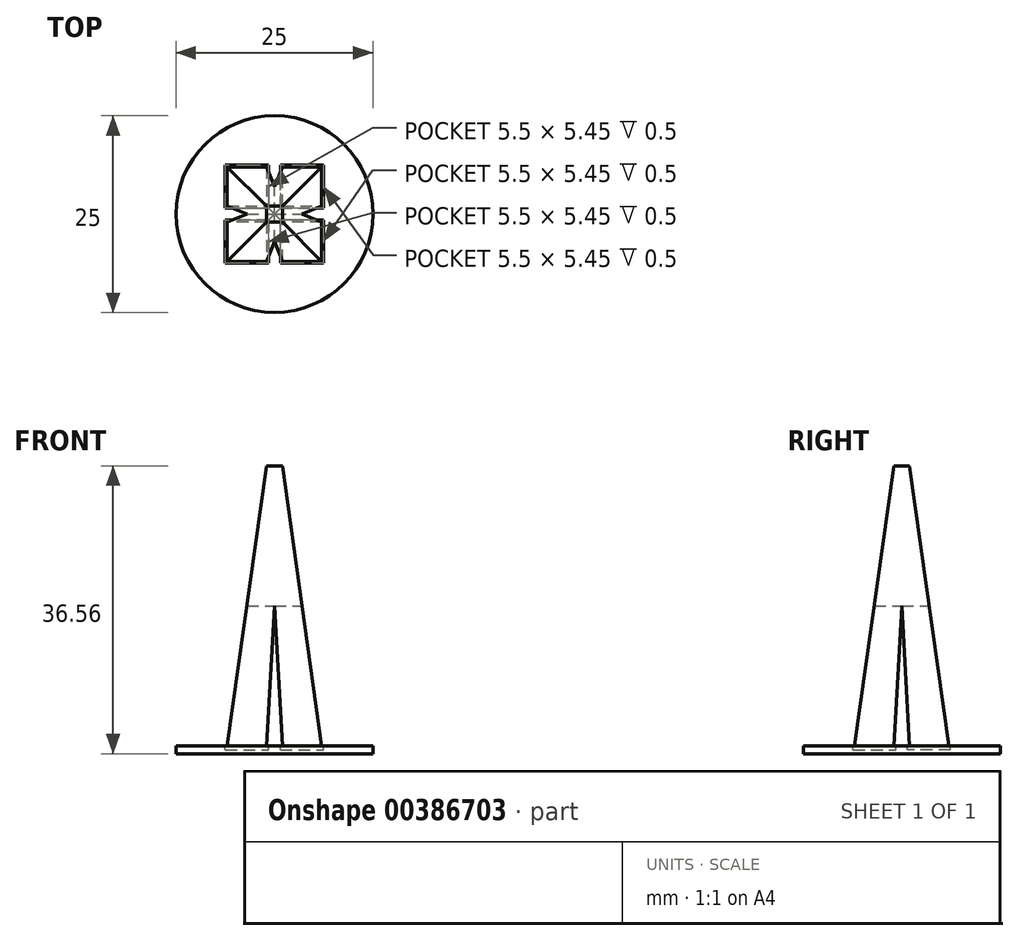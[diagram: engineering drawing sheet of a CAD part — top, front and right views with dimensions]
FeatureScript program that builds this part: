
annotation { "Feature Type Name" : "Feature", "Feature Type Description" : "" }
export const myFeature = defineFeature(function(context is Context, id is Id, definition is map)
    precondition{}
    {
        {
            var Q0;
            Q0=qCreatedBy(makeId("Top.planeOp"),FACE);
            var sketch = newSketch(context, id + "F0", { "sketchPlane" : qUnion([Q0])});
            skLineSegment(sketch, "E0.bottom", {"start": v(-6, 6) * mm, "end": v(6, 6) * mm});
            skLineSegment(sketch, "E0.top", {"start": v(-6, -6) * mm, "end": v(6, -6) * mm});
            skLineSegment(sketch, "E0.left", {"start": v(-6, 6) * mm, "end": v(-6, -6) * mm});
            skLineSegment(sketch, "E0.right", {"start": v(6, 6) * mm, "end": v(6, -6) * mm});
            skPoint(sketch, "E0.middle", {"position": v(0, 0) * mm});
            skLineSegment(sketch, "E1", {"start": v(-6, 0) * mm, "end": v(6, 0) * mm});
            skLineSegment(sketch, "E2", {"start": v(0, 6) * mm, "end": v(0, -6) * mm});
            skLineSegment(sketch, "E3", {"start": v(-1, 6) * mm, "end": v(-1, -6) * mm});
            skLineSegment(sketch, "E4", {"start": v(1, -6) * mm, "end": v(1, 6) * mm});
            skLineSegment(sketch, "E5", {"start": v(-6, 1) * mm, "end": v(6, 1) * mm});
            skLineSegment(sketch, "E6", {"start": v(6, -1) * mm, "end": v(-6, -1) * mm});
            skSolve(sketch);
        }
        {
            var Q0;
            Q0=qCreatedBy(makeId("Top.planeOp"),FACE);
            cPlane(context, id + "F1", {"entities" : qUnion([Q0]), "cplaneType" : CPlaneType.OFFSET, "offset" : 35.56 * mm, "width" : 150 * mm, "height" : 150 * mm});
        }
        {
            var Q0;
            Q0=qCreatedBy(id+"F1.planeOp",FACE);
            var sketch = newSketch(context, id + "F2", { "sketchPlane" : qUnion([Q0])});
            skLineSegment(sketch, "E7.bottom", {"start": v(-1, 1) * mm, "end": v(1, 1) * mm});
            skLineSegment(sketch, "E7.top", {"start": v(-1, -1) * mm, "end": v(1, -1) * mm});
            skLineSegment(sketch, "E7.left", {"start": v(-1, 1) * mm, "end": v(-1, -1) * mm});
            skLineSegment(sketch, "E7.right", {"start": v(1, 1) * mm, "end": v(1, -1) * mm});
            skPoint(sketch, "E7.middle", {"position": v(0, 0) * mm});
            skSolve(sketch);
        }
        {
            var Q0;
            {var subQ0=sQuery(id+"F0.wireOp",EDGE,"E0.left");var subQ1=sQuery(id+"F0.wireOp",EDGE,"E0.bottom");var subQ2=makeQuery(id+"F0.imprint","INTERSECT",VERTEX,{"derivedFrom":[subQ1,subQ0]});Q0=makeQuery(id+"F0.imprint","IMPRINT",FACE,{"disambiguationData":[TD([[makeQuery(id+"F0.imprint","IMPRINT",EDGE,{"disambiguationData":[TD([[subQ2,-1.0]])],"derivedFrom":subQ1}),-1.0]])]});}
            var Q1;
            Q1=makeQuery(id+"F2.imprint","IMPRINT",FACE,{"disambiguationData":[TD([[makeQuery(id+"F2.imprint","IMPRINT",EDGE,{"derivedFrom":sQuery(id+"F2.wireOp",EDGE,"E7.bottom")}),-1.0]])]});
            loft(context, id + "F3", {"sheetProfilesArray" : [{ "sheetProfileEntities" : qUnion([Q0]) }, { "sheetProfileEntities" : qUnion([Q1]) }]});
        }
        {
            var Q0;
            Q0=qCreatedBy(makeId("Top.planeOp"),FACE);
            var sketch = newSketch(context, id + "F4", { "sketchPlane" : qUnion([Q0])});
            skCircle(sketch, "E8", {"center": v(0, 0) * mm, "radius": 12.5 * mm});
            skSolve(sketch);
        }
        {
            var Q0;
            Q0=makeQuery(id+"F4.imprint","IMPRINT",FACE,{"disambiguationData":[TD([[makeQuery(id+"F4.imprint","IMPRINT",EDGE,{"derivedFrom":sQuery(id+"F4.wireOp",EDGE,"E8")}),1.0]])]});
            extrude(context, id + "F5", {"entities" : qUnion([Q0]), "oppositeDirection" : true, "depth" : 1 * mm});
        }
        {
            var Q0;
            Q0=makeQuery(id+"F5.opExtrude","CAP_FACE",FACE,{"disambiguationData":[OSD([sQuery(id+"F4.wireOp",EDGE,"E8")])],"isStart":true});
            var sketch = newSketch(context, id + "F6", { "sketchPlane" : qUnion([Q0])});
            skLineSegment(sketch, "E9.bottom", {"start": v(-6.25, 6.2) * mm, "end": v(6.25, 6.2) * mm});
            skLineSegment(sketch, "E9.top", {"start": v(-6.25, -6.2) * mm, "end": v(6.25, -6.2) * mm});
            skLineSegment(sketch, "E9.left", {"start": v(-6.25, 6.2) * mm, "end": v(-6.25, -6.2) * mm});
            skLineSegment(sketch, "E9.right", {"start": v(6.25, 6.2) * mm, "end": v(6.25, -6.2) * mm});
            skPoint(sketch, "E9.middle", {"position": v(0, 0) * mm});
            skLineSegment(sketch, "E10", {"start": v(0, 6.2) * mm, "end": v(0, -6.2) * mm});
            skLineSegment(sketch, "E11", {"start": v(-6.25, 0) * mm, "end": v(6.25, 0) * mm});
            skLineSegment(sketch, "E12", {"start": v(-0.75, 6.2) * mm, "end": v(-0.75, -6.2) * mm});
            skLineSegment(sketch, "E13", {"start": v(0.75, -6.2) * mm, "end": v(0.75, 6.2) * mm});
            skLineSegment(sketch, "E14", {"start": v(-6.25, 0.75) * mm, "end": v(6.25, 0.75) * mm});
            skLineSegment(sketch, "E15", {"start": v(6.25, -0.75) * mm, "end": v(-6.25, -0.75) * mm});
            skSolve(sketch);
        }
        {
            var Q0;
            {var subQ0=sQuery(id+"F6.wireOp",EDGE,"E9.left");var subQ1=sQuery(id+"F6.wireOp",EDGE,"E9.bottom");var subQ2=makeQuery(id+"F6.imprint","INTERSECT",VERTEX,{"derivedFrom":[subQ1,subQ0]});Q0=makeQuery(id+"F6.imprint","IMPRINT",FACE,{"disambiguationData":[TD([[makeQuery(id+"F6.imprint","IMPRINT",EDGE,{"disambiguationData":[TD([[subQ2,-1.0]])],"derivedFrom":subQ1}),-1.0]])]});}
            var Q1;
            {var subQ0=sQuery(id+"F6.wireOp",EDGE,"E9.right");var subQ1=sQuery(id+"F6.wireOp",EDGE,"E9.bottom");var subQ2=makeQuery(id+"F6.imprint","INTERSECT",VERTEX,{"derivedFrom":[subQ1,subQ0]});Q1=makeQuery(id+"F6.imprint","IMPRINT",FACE,{"disambiguationData":[TD([[makeQuery(id+"F6.imprint","IMPRINT",EDGE,{"disambiguationData":[TD([[subQ2,1.0]])],"derivedFrom":subQ1}),-1.0]])]});}
            var Q2;
            {var subQ0=sQuery(id+"F6.wireOp",EDGE,"E9.left");var subQ1=sQuery(id+"F6.wireOp",EDGE,"E9.top");var subQ2=makeQuery(id+"F6.imprint","INTERSECT",VERTEX,{"derivedFrom":[subQ1,subQ0]});Q2=makeQuery(id+"F6.imprint","IMPRINT",FACE,{"disambiguationData":[TD([[makeQuery(id+"F6.imprint","IMPRINT",EDGE,{"disambiguationData":[TD([[subQ2,-1.0]])],"derivedFrom":subQ1}),1.0]])]});}
            var Q3;
            {var subQ0=sQuery(id+"F6.wireOp",EDGE,"E9.right");var subQ1=sQuery(id+"F6.wireOp",EDGE,"E9.top");var subQ2=makeQuery(id+"F6.imprint","INTERSECT",VERTEX,{"derivedFrom":[subQ1,subQ0]});Q3=makeQuery(id+"F6.imprint","IMPRINT",FACE,{"disambiguationData":[TD([[makeQuery(id+"F6.imprint","IMPRINT",EDGE,{"disambiguationData":[TD([[subQ2,1.0]])],"derivedFrom":subQ1}),1.0]])]});}
            extrude(context, id + "F7", {"entities" : qUnion([Q0, Q1, Q2, Q3]), "operationType" : NewBodyOperationType.REMOVE, "oppositeDirection" : true, "depth" : .5 * mm});
        }
        {
            var Q1;
            Q1 = qSketchRegion(id + "F2", true);
            var Q2;
            {var subQ0=sQuery(id+"F0.wireOp",EDGE,"E0.left");var subQ1=sQuery(id+"F0.wireOp",EDGE,"E0.top");var subQ2=makeQuery(id+"F0.imprint","INTERSECT",VERTEX,{"derivedFrom":[subQ1,subQ0]});Q2=makeQuery(id+"F0.imprint","IMPRINT",FACE,{"disambiguationData":[TD([[makeQuery(id+"F0.imprint","IMPRINT",EDGE,{"disambiguationData":[TD([[subQ2,-1.0]])],"derivedFrom":subQ1}),1.0]])]});}
            loft(context, id + "F8", {"operationType" : NewBodyOperationType.ADD, "sheetProfilesArray" : [{ "sheetProfileEntities" : qUnion([Q1]) }, { "sheetProfileEntities" : qUnion([Q2]) }]});
        }
        {
            var Q1;
            {var subQ0=sQuery(id+"F0.wireOp",EDGE,"E0.right");var subQ1=sQuery(id+"F0.wireOp",EDGE,"E0.bottom");var subQ2=makeQuery(id+"F0.imprint","INTERSECT",VERTEX,{"derivedFrom":[subQ1,subQ0]});Q1=makeQuery(id+"F0.imprint","IMPRINT",FACE,{"disambiguationData":[TD([[makeQuery(id+"F0.imprint","IMPRINT",EDGE,{"disambiguationData":[TD([[subQ2,1.0]])],"derivedFrom":subQ1}),-1.0]])]});}
            var Q2;
            Q2=makeQuery(id+"F3.opLoft","CAP_FACE",FACE,{"disambiguationData":[OSD([makeQuery(id+"F2.imprint","IMPRINT",FACE,{"disambiguationData":[TD([[makeQuery(id+"F2.imprint","IMPRINT",EDGE,{"derivedFrom":sQuery(id+"F2.wireOp",EDGE,"E7.bottom")}),-1.0]])]})])],"isStart":true});
            loft(context, id + "F9", {"operationType" : NewBodyOperationType.ADD, "sheetProfilesArray" : [{ "sheetProfileEntities" : qUnion([Q1]) }, { "sheetProfileEntities" : qUnion([Q2]) }]});
        }
        {
            var Q1;
            {var subQ0=sQuery(id+"F0.wireOp",EDGE,"E0.right");var subQ1=sQuery(id+"F0.wireOp",EDGE,"E0.top");var subQ2=makeQuery(id+"F0.imprint","INTERSECT",VERTEX,{"derivedFrom":[subQ1,subQ0]});Q1=makeQuery(id+"F0.imprint","IMPRINT",FACE,{"disambiguationData":[TD([[makeQuery(id+"F0.imprint","IMPRINT",EDGE,{"disambiguationData":[TD([[subQ2,1.0]])],"derivedFrom":subQ1}),1.0]])]});}
            var Q2;
            Q2=makeQuery(id+"F3.opLoft","CAP_FACE",FACE,{"disambiguationData":[OSD([makeQuery(id+"F2.imprint","IMPRINT",FACE,{"disambiguationData":[TD([[makeQuery(id+"F2.imprint","IMPRINT",EDGE,{"derivedFrom":sQuery(id+"F2.wireOp",EDGE,"E7.bottom")}),-1.0]])]})])],"isStart":true});
            loft(context, id + "F10", {"operationType" : NewBodyOperationType.ADD, "sheetProfilesArray" : [{ "sheetProfileEntities" : qUnion([Q1]) }, { "sheetProfileEntities" : qUnion([Q2]) }]});
        }
    });
